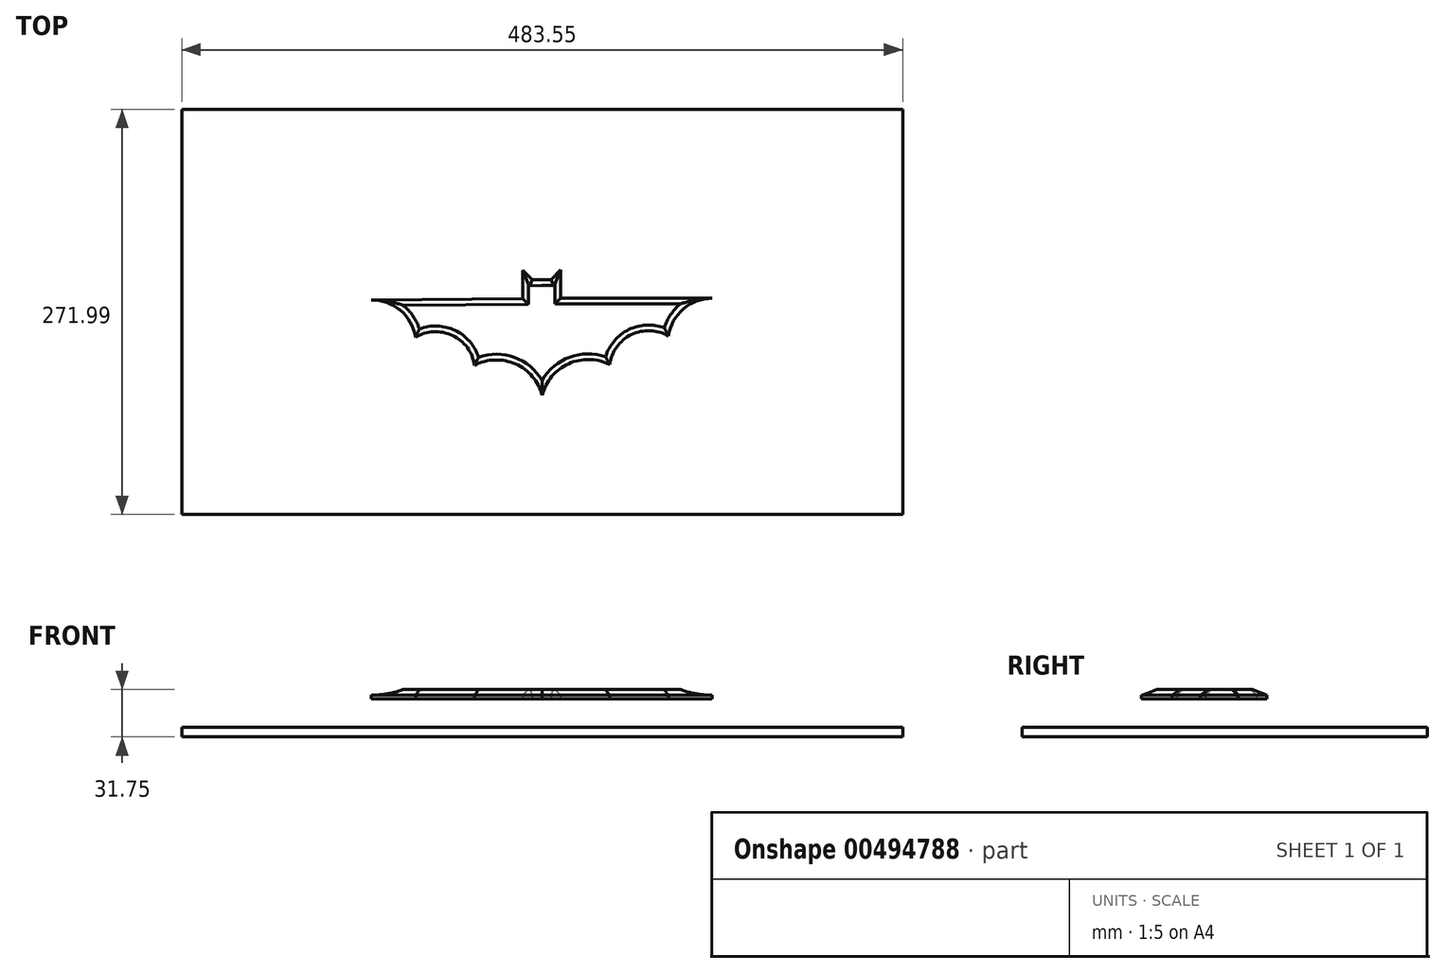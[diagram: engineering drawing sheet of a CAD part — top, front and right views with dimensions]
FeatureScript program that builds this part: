
annotation { "Feature Type Name" : "Feature", "Feature Type Description" : "" }
export const myFeature = defineFeature(function(context is Context, id is Id, definition is map)
    precondition{}
    {
        {
            var Q0;
            Q0=qCreatedBy(makeId("Top.planeOp"),FACE);
            var sketch = newSketch(context, id + "F0", { "sketchPlane" : qUnion([Q0])});
            skLineSegment(sketch, "E0", {"start": v(-89.28, 9.07) * mm, "end": v(-13.08, 9.07) * mm});
            skLineSegment(sketch, "E1", {"start": v(-13.08, 9.07) * mm, "end": v(-13.08, 28.12) * mm});
            skLineSegment(sketch, "E2", {"start": v(-13.08, 28.12) * mm, "end": v(-6.73, 21.45) * mm});
            skLineSegment(sketch, "E3", {"start": v(-6.73, 21.45) * mm, "end": v(5.97, 21.45) * mm});
            skLineSegment(sketch, "E4", {"start": v(5.97, 21.45) * mm, "end": v(12.32, 28.12) * mm});
            skLineSegment(sketch, "E5", {"start": v(12.32, 28.12) * mm, "end": v(12.32, 9.07) * mm});
            skLineSegment(sketch, "E6", {"start": v(12.32, 9.07) * mm, "end": v(113.92, 9.07) * mm});
            skLineSegment(sketch, "E7", {"start": v(-0.38, 21.45) * mm, "end": v(0, -55.89) * mm});
            skArc(sketch, "E8", {"start": v(45.2, -35.36) * mm, "mid": v(17.7, -34.82) * mm, "end": v(0, -55.89) * mm});
            skArc(sketch, "E9", {"start": v(84.59, -16.23) * mm, "mid": v(59.8, -15.3) * mm, "end": v(45.2, -35.36) * mm});
            skArc(sketch, "E10", {"start": v(113.92, 9.07) * mm, "mid": v(94.55, 1.87) * mm, "end": v(84.59, -16.23) * mm});
            skSolve(sketch);
        }
        {
            var Q0;
            {var subQ0=sQuery(id+"F0.wireOp",EDGE,"E4");Q0=makeQuery(id+"F0.imprint","IMPRINT",FACE,{"disambiguationData":[TD([[makeQuery(id+"F0.imprint","IMPRINT",EDGE,{"derivedFrom":subQ0}),-1.0]])]});}
            extrude(context, id + "F1", {"entities" : qUnion([Q0]), "depth" : 6.35 * mm});
        }
        {
            var Q0;
            Q0=makeQuery(id+"F1.opExtrude","SWEPT_BODY",BODY,{"disambiguationData":[OSD([sQuery(id+"F0.wireOp",EDGE,"E3"),sQuery(id+"F0.wireOp",EDGE,"E4"),sQuery(id+"F0.wireOp",EDGE,"E5"),sQuery(id+"F0.wireOp",EDGE,"E6"),sQuery(id+"F0.wireOp",EDGE,"E7"),sQuery(id+"F0.wireOp",EDGE,"E8"),sQuery(id+"F0.wireOp",EDGE,"E9"),sQuery(id+"F0.wireOp",EDGE,"E10")])]});
            var Q1;
            Q1=makeQuery(id+"F1.opExtrude","SWEPT_FACE",FACE,{"disambiguationData":[OSD([sQuery(id+"F0.wireOp",EDGE,"E7")])]});
            mirror(context, id + "F2", {"operationType" : NewBodyOperationType.ADD, "entities" : qUnion([Q0]), "mirrorPlane" : qUnion([Q1])});
        }
        {
            var Q0;
            {var subQ0=makeQuery(id+"F1.opExtrude","CAP_FACE",FACE,{"disambiguationData":[OSD([sQuery(id+"F0.wireOp",EDGE,"E3"),sQuery(id+"F0.wireOp",EDGE,"E4"),sQuery(id+"F0.wireOp",EDGE,"E5"),sQuery(id+"F0.wireOp",EDGE,"E6"),sQuery(id+"F0.wireOp",EDGE,"E7"),sQuery(id+"F0.wireOp",EDGE,"E8"),sQuery(id+"F0.wireOp",EDGE,"E9"),sQuery(id+"F0.wireOp",EDGE,"E10")])],"isStart":false});Q0=makeQuery(id+"F2.boolean.opBoolean","MERGE",FACE,{"derivedFrom":[subQ0,makeQuery(id+"F2.opPattern","COPY",FACE,{"derivedFrom":subQ0,"instanceName":"1"})]});}
            chamfer(context, id + "F3", {"entities" : qUnion([Q0]), "width" : 3.8 * mm, "tangentPropagation" : true});
        }
        {
            var Q0;
            Q0=qCreatedBy(makeId("Top.planeOp"),FACE);
            cPlane(context, id + "F4", {"entities" : qUnion([Q0]), "cplaneType" : CPlaneType.OFFSET, "offset" : 25.4 * mm, "oppositeDirection" : true, "width" : 152.4 * mm, "height" : 152.4 * mm});
        }
        {
            var Q0;
            Q0=qCreatedBy(id+"F4.planeOp",FACE);
            var sketch = newSketch(context, id + "F5", { "sketchPlane" : qUnion([Q0])});
            skLineSegment(sketch, "E11.bottom", {"start": v(-241.77, -136) * mm, "end": v(241.78, -136) * mm});
            skLineSegment(sketch, "E11.top", {"start": v(-241.77, 136) * mm, "end": v(241.78, 136) * mm});
            skLineSegment(sketch, "E11.left", {"start": v(-241.77, -136) * mm, "end": v(-241.77, 136) * mm});
            skLineSegment(sketch, "E11.right", {"start": v(241.78, -136) * mm, "end": v(241.78, 136) * mm});
            skSolve(sketch);
        }
        {
            var Q0;
            Q0=qSketchRegion(id+"F5",true);
            extrude(context, id + "F6", {"entities" : qUnion([Q0]), "depth" : 6.35 * mm});
        }
    });
